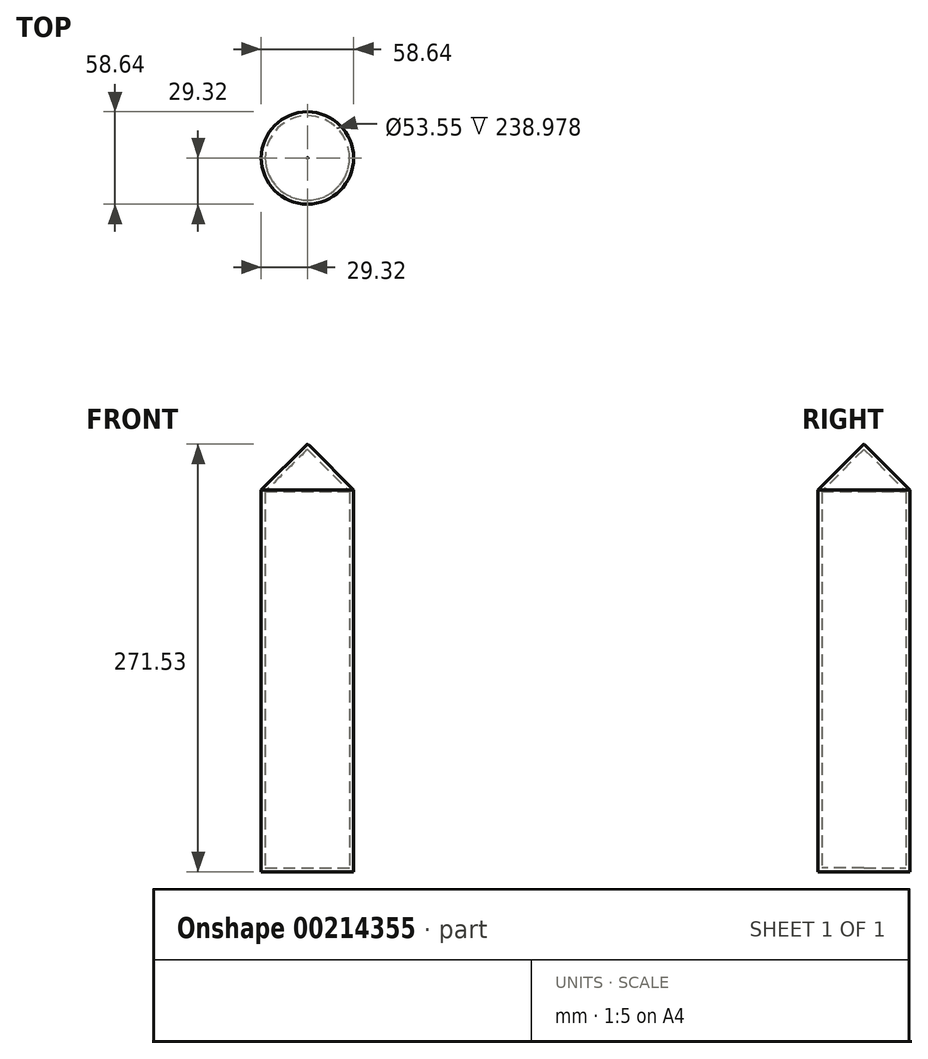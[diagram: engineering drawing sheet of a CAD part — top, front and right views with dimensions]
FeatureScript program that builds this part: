
annotation { "Feature Type Name" : "Feature", "Feature Type Description" : "" }
export const myFeature = defineFeature(function(context is Context, id is Id, definition is map)
    precondition{}
    {
        {
            var Q0;
            Q0=qCreatedBy(makeId("Top.planeOp"),FACE);
            var sketch = newSketch(context, id + "F0", { "sketchPlane" : qUnion([Q0])});
            skCircle(sketch, "E0", {"center": v(0, 0) * mm, "radius": 29.32 * mm});
            skSolve(sketch);
        }
        {
            var Q0;
            Q0=makeQuery(id+"F0.imprint","IMPRINT",FACE,{"disambiguationData":[TD([[makeQuery(id+"F0.imprint","IMPRINT",EDGE,{"derivedFrom":sQuery(id+"F0.wireOp",EDGE,"E0")}),1.0]])]});
            extrude(context, id + "F1", {"entities" : qUnion([Q0]), "depth" : 68.33 * mm});
        }
        {
            var Q0;
            Q0=makeQuery(id+"F1.opExtrude","CAP_FACE",FACE,{"disambiguationData":[OSD([sQuery(id+"F0.wireOp",EDGE,"E0")])],"isStart":false});
            extrude(context, id + "F2", {"entities" : qUnion([Q0]), "operationType" : NewBodyOperationType.ADD, "depth" : 203.2 * mm, "hasDraft" : true, "draftAngle" : 0 * degree});
        }
        {
            var Q0;
            Q0=makeQuery(id+"F2.opExtrude","CAP_FACE",FACE,{"disambiguationData":[OSD([sQuery(id+"F0.wireOp",EDGE,"E0")])],"isStart":false});
            chamfer(context, id + "F3", {"entities" : qUnion([Q0]), "width" : 28.96 * mm, "tangentPropagation" : true});
        }
        {
            var Q0;
            {var subQ0=sQuery(id+"F0.wireOp",EDGE,"E0");Q0=makeQuery(id+"F2.boolean.opBoolean","MERGE",FACE,{"derivedFrom":[makeQuery(id+"F1.opExtrude","SWEPT_FACE",FACE,{"disambiguationData":[OSD([subQ0])]}),makeQuery(id+"F2.opExtrude","SWEPT_FACE",FACE,{"disambiguationData":[OSD([subQ0])]})]});}
            var Q1;
            Q1=makeQuery(id+"F1.opExtrude","SWEPT_BODY",BODY,{"disambiguationData":[OSD([sQuery(id+"F0.wireOp",EDGE,"E0")])]});
            shell(context, id + "F4", {"isHollow" : true, "entities" : qUnion([Q0]), "parts" : qUnion([Q1]), "thickness" : 2.54 * mm});
        }
    });
